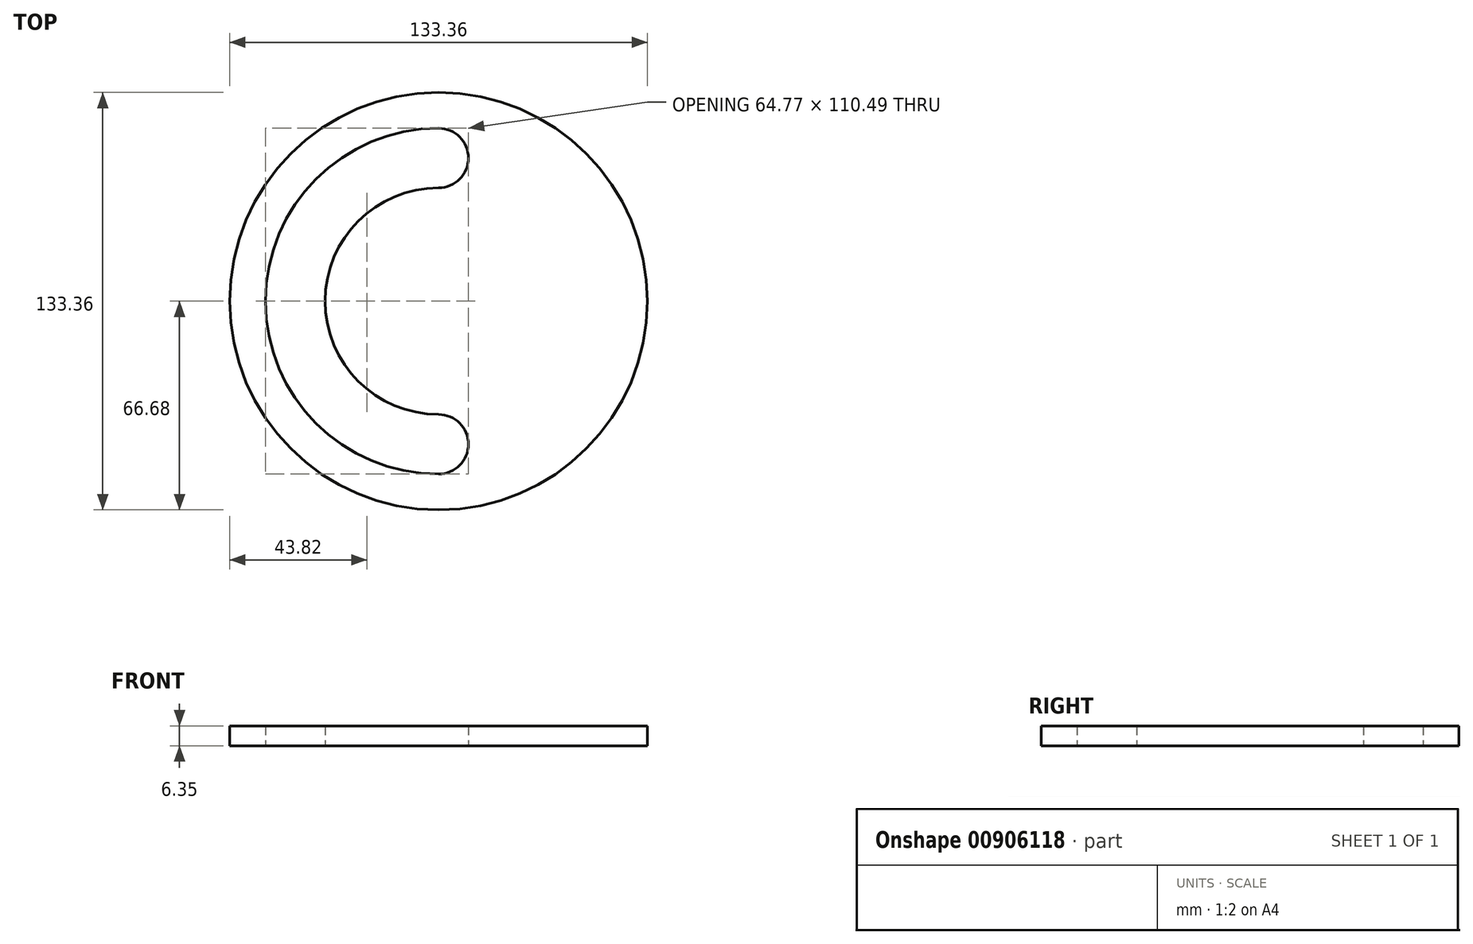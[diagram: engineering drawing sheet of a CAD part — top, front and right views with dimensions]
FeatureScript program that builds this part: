
annotation { "Feature Type Name" : "Feature", "Feature Type Description" : "" }
export const myFeature = defineFeature(function(context is Context, id is Id, definition is map)
    precondition{}
    {
        {
            var Q0;
            Q0=qCreatedBy(makeId("Top.planeOp"),FACE);
            var sketch = newSketch(context, id + "F0", { "sketchPlane" : qUnion([Q0])});
            skCircle(sketch, "E0", {"center": v(0, 0) * mm, "radius": 25.4 * mm});
            skCircle(sketch, "E1.cCircle", {"center": v(0, 0) * mm, "radius": 42.94 * mm, "construction": true});
            skLineSegment(sketch, "E1.0", {"start": v(0, 44.45) * mm, "end": v(22.23, 38.5) * mm, "construction": true});
            skLineSegment(sketch, "E1.1", {"start": v(22.22, 38.5) * mm, "end": v(38.5, 22.23) * mm, "construction": true});
            skLineSegment(sketch, "E1.2", {"start": v(38.5, 22.23) * mm, "end": v(44.45, 0) * mm, "construction": true});
            skLineSegment(sketch, "E1.3", {"start": v(44.45, 0) * mm, "end": v(38.5, -22.22) * mm, "construction": true});
            skLineSegment(sketch, "E1.4", {"start": v(38.5, -22.22) * mm, "end": v(22.23, -38.5) * mm, "construction": true});
            skLineSegment(sketch, "E1.5", {"start": v(22.23, -38.5) * mm, "end": v(0, -44.45) * mm, "construction": true});
            skLineSegment(sketch, "E1.6", {"start": v(0, -44.45) * mm, "end": v(-22.22, -38.5) * mm, "construction": true});
            skLineSegment(sketch, "E1.7", {"start": v(-22.22, -38.5) * mm, "end": v(-38.5, -22.23) * mm, "construction": true});
            skLineSegment(sketch, "E1.8", {"start": v(-38.5, -22.23) * mm, "end": v(-44.45, 0) * mm, "construction": true});
            skLineSegment(sketch, "E1.9", {"start": v(-44.45, 0) * mm, "end": v(-38.5, 22.22) * mm, "construction": true});
            skLineSegment(sketch, "E1.10", {"start": v(-38.5, 22.22) * mm, "end": v(-22.23, 38.5) * mm, "construction": true});
            skLineSegment(sketch, "E1.11", {"start": v(-22.23, 38.5) * mm, "end": v(0, 44.45) * mm, "construction": true});
            skPoint(sketch, "E1.0.midPoint", {"position": v(11.11, 41.47) * mm});
            skCircle(sketch, "E2", {"center": v(22.22, 38.5) * mm, "radius": 9.53 * mm});
            skCircle(sketch, "E3", {"center": v(38.5, 22.23) * mm, "radius": 9.53 * mm});
            skCircle(sketch, "E4", {"center": v(44.45, 0) * mm, "radius": 9.53 * mm});
            skCircle(sketch, "E5", {"center": v(38.5, -22.22) * mm, "radius": 9.53 * mm});
            skCircle(sketch, "E6", {"center": v(22.23, -38.5) * mm, "radius": 9.53 * mm});
            skPoint(sketch, "E7.startSnap0", {"position": v(-41.47, 11.11) * mm});
            skArc(sketch, "E8", {"start": v(0, 45.72) * mm, "mid": v(-45.72, 0) * mm, "end": v(0, -45.72) * mm, "construction": true});
            skArc(sketch, "E9.0.startCap", {"start": v(0, 55.25) * mm, "mid": v(9.53, 45.72) * mm, "end": v(0, 36.2) * mm});
            skArc(sketch, "E9.0.endCap", {"start": v(0, -36.2) * mm, "mid": v(9.52, -45.72) * mm, "end": v(0, -55.24) * mm});
            skArc(sketch, "E9.0.left", {"start": v(0, 36.2) * mm, "mid": v(-36.2, 0) * mm, "end": v(0, -36.2) * mm});
            skArc(sketch, "E9.0.right", {"start": v(0, 55.25) * mm, "mid": v(-55.25, 0) * mm, "end": v(0, -55.25) * mm});
            skCircle(sketch, "E10", {"center": v(0, 0) * mm, "radius": 66.68 * mm});
            skCircle(sketch, "E11.0", {"center": v(0, 0) * mm, "radius": 73.03 * mm});
            skPoint(sketch, "E12", {"position": v(25.4, 0) * mm});
            skPoint(sketch, "E13", {"position": v(-25.4, 0) * mm});
            skSolve(sketch);
        }
        {
            var Q0;
            Q0=makeQuery(id+"F0.imprint","IMPRINT",FACE,{"disambiguationData":[TD([[makeQuery(id+"F0.imprint","IMPRINT",EDGE,{"derivedFrom":sQuery(id+"F0.wireOp",EDGE,"E9.0.startCap")}),-1.0]])]});
            var Q1;
            Q1=makeQuery(id+"F0.imprint","IMPRINT",FACE,{"disambiguationData":[TD([[makeQuery(id+"F0.imprint","IMPRINT",EDGE,{"derivedFrom":sQuery(id+"F0.wireOp",EDGE,"E0")}),1.0]])]});
            var Q2;
            Q2=makeQuery(id+"F0.imprint","IMPRINT",FACE,{"disambiguationData":[TD([[makeQuery(id+"F0.imprint","IMPRINT",EDGE,{"derivedFrom":sQuery(id+"F0.wireOp",EDGE,"E6")}),1.0]])]});
            var Q3;
            Q3=makeQuery(id+"F0.imprint","IMPRINT",FACE,{"disambiguationData":[TD([[makeQuery(id+"F0.imprint","IMPRINT",EDGE,{"derivedFrom":sQuery(id+"F0.wireOp",EDGE,"E5")}),1.0]])]});
            var Q4;
            Q4=makeQuery(id+"F0.imprint","IMPRINT",FACE,{"disambiguationData":[TD([[makeQuery(id+"F0.imprint","IMPRINT",EDGE,{"derivedFrom":sQuery(id+"F0.wireOp",EDGE,"E4")}),1.0]])]});
            var Q5;
            Q5=makeQuery(id+"F0.imprint","IMPRINT",FACE,{"disambiguationData":[TD([[makeQuery(id+"F0.imprint","IMPRINT",EDGE,{"derivedFrom":sQuery(id+"F0.wireOp",EDGE,"E3")}),1.0]])]});
            var Q6;
            Q6=makeQuery(id+"F0.imprint","IMPRINT",FACE,{"disambiguationData":[TD([[makeQuery(id+"F0.imprint","IMPRINT",EDGE,{"derivedFrom":sQuery(id+"F0.wireOp",EDGE,"E2")}),1.0]])]});
            extrude(context, id + "F1", {"entities" : qUnion([Q0, Q1, Q2, Q3, Q4, Q5, Q6]), "depth" : 6.35 * mm, "offsetDistance" : 25.4 * mm});
        }
    });
